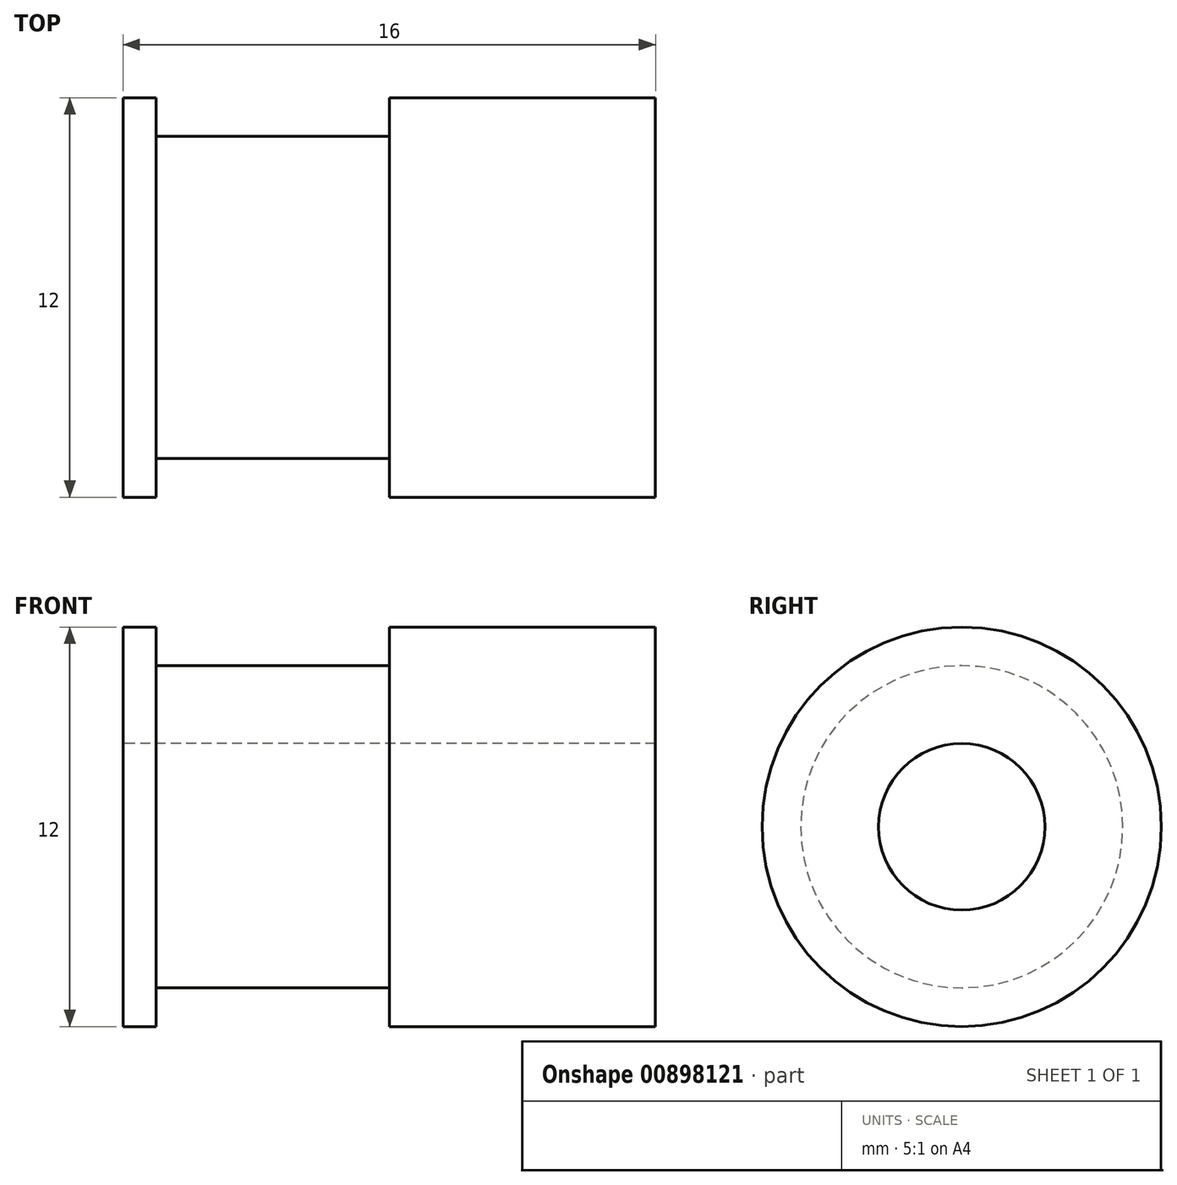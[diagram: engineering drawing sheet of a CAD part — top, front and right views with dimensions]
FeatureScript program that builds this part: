
annotation { "Feature Type Name" : "Feature", "Feature Type Description" : "" }
export const myFeature = defineFeature(function(context is Context, id is Id, definition is map)
    precondition{}
    {
        {
            var Q0;
            Q0=qCreatedBy(makeId("Front.planeOp"),FACE);
            var sketch = newSketch(context, id + "F0", { "sketchPlane" : qUnion([Q0])});
            skLineSegment(sketch, "E0", {"start": v(-17.32, 0) * mm, "end": v(19.17, 0) * mm});
            skLineSegment(sketch, "E1", {"start": v(-10.67, 2.5) * mm, "end": v(5.33, 2.5) * mm});
            skLineSegment(sketch, "E2", {"start": v(5.33, 2.5) * mm, "end": v(5.33, 6) * mm});
            skLineSegment(sketch, "E3", {"start": v(5.33, 6) * mm, "end": v(-2.67, 6) * mm});
            skLineSegment(sketch, "E4", {"start": v(-2.67, 6) * mm, "end": v(-2.67, 4.84) * mm});
            skLineSegment(sketch, "E5", {"start": v(-2.67, 4.84) * mm, "end": v(-9.67, 4.84) * mm});
            skLineSegment(sketch, "E6", {"start": v(-9.67, 4.84) * mm, "end": v(-9.67, 6) * mm});
            skLineSegment(sketch, "E7", {"start": v(-9.67, 6) * mm, "end": v(-10.67, 6) * mm});
            skLineSegment(sketch, "E8", {"start": v(-10.67, 6) * mm, "end": v(-10.67, 2.5) * mm});
            skSolve(sketch);
        }
        {
            var Q0;
            Q0 = qSketchRegion(id + "F0", true);
            var Q1;
            Q1=sQuery(id+"F0.wireOp",EDGE,"E0");
            revolve(context, id + "F1", {"surfaceOperationType" : NewSurfaceOperationType.NEW, "entities" : qUnion([Q0]), "axis" : qUnion([Q1]), "revolveType" : RevolveType.FULL});
        }
    });
